# Revit family: EMILYK1508 - Emily 2 Seater Settee
name_source: partatom
category: Furniture
revit_build: Autodesk Revit 2014 (Build: 20131024_2115(x64)
units: mm (PartAtom-declared; Revit-internal decimal feet)

## types (1)
- EMILYK1508 - Emily Two Seater Settee-1200w x 740d x 485(sh) x 1100mm o/a Height
    CatRef = EMILY1508
    CatURL = http://www.knightsbridge-furniture.co.uk
    Description = Emily Two Seater Settee
    Dim 1 (W) = 1200 mm
    Dim 2 (D) = 740 mm
    Dim 3 (H) = 485 mm  [stored 1.59121 ft]
    Finish & Fabrics = http://www.knightsbridge-furniture.co.uk
    Manufacturer = Knightsbridge Furniture Productions Ltd.
    Model = Settee
    Product Range = Lounge Seating
    Type Comments = Ergonomically designed to aid good posture
    URL = http://www.knightsbridge-furniture.co.uk
    o/a Height = 1100 mm

note: [stored X ft] marks values corroborated as IEEE doubles in the binary element streams (Revit-internal decimal feet)

## geometry (parser evidence)
native form markers: Sweep x2
no freeform markers — native parametric forms only
